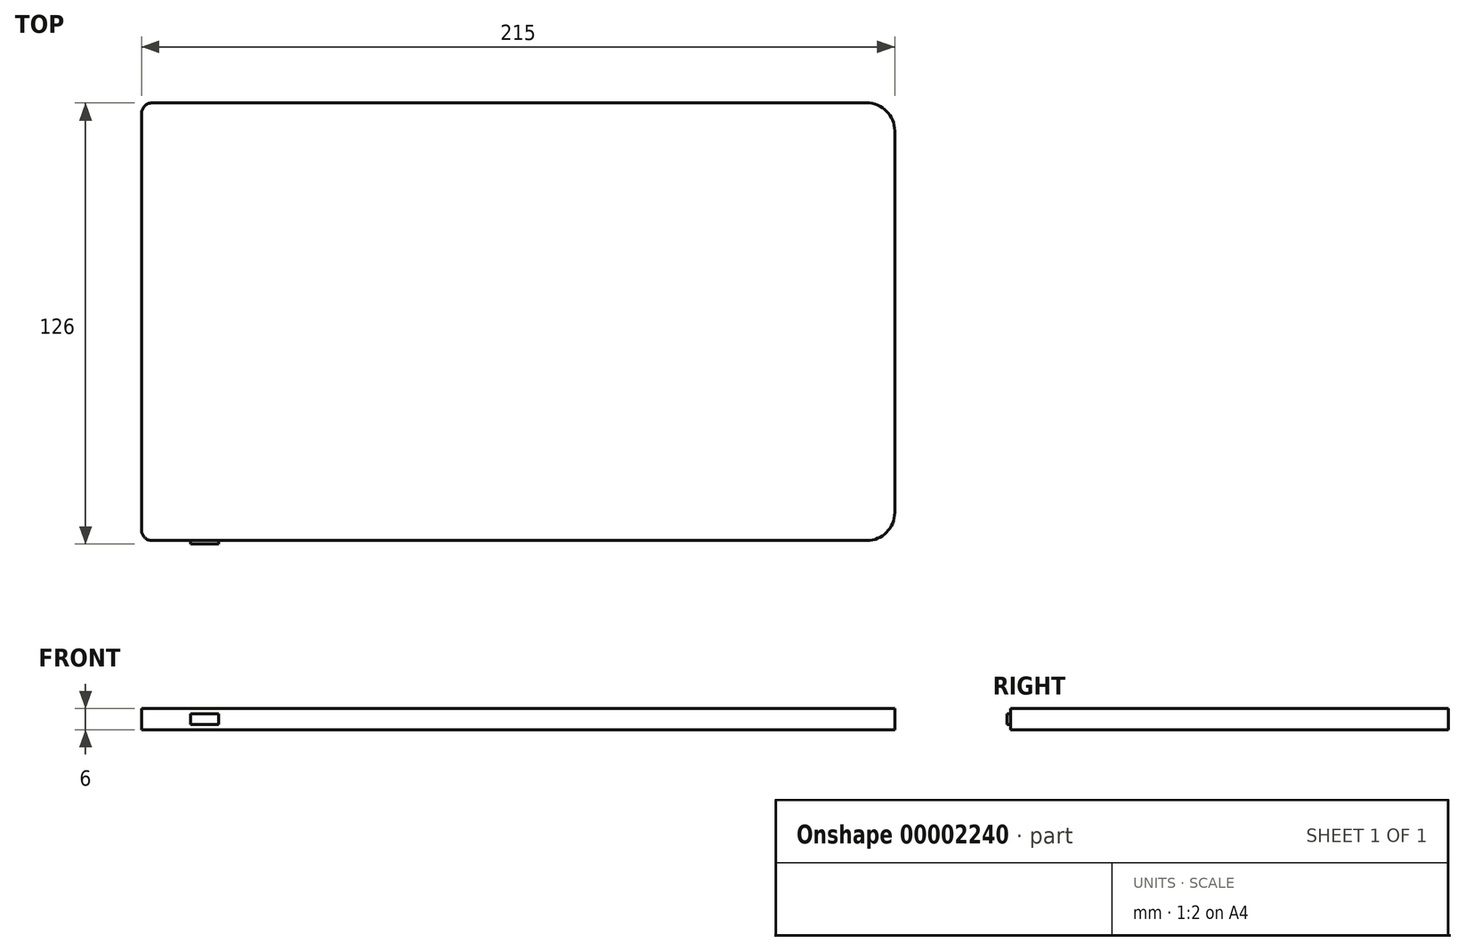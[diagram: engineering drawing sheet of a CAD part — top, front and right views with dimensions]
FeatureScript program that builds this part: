
annotation { "Feature Type Name" : "Feature", "Feature Type Description" : "" }
export const myFeature = defineFeature(function(context is Context, id is Id, definition is map)
    precondition{}
    {
        {
            var Q0;
            Q0=qCreatedBy(makeId("Top.planeOp"),FACE);
            var sketch = newSketch(context, id + "F0", { "sketchPlane" : qUnion([Q0])});
            skLineSegment(sketch, "E0.bottom", {"start": v(3, 125) * mm, "end": v(207, 125) * mm});
            skLineSegment(sketch, "E0.top", {"start": v(3, 0) * mm, "end": v(207, 0) * mm});
            skLineSegment(sketch, "E0.left", {"start": v(0, 122) * mm, "end": v(0, 3) * mm});
            skLineSegment(sketch, "E0.right", {"start": v(215, 117) * mm, "end": v(215, 8) * mm});
            skPoint(sketch, "E1.visualSharp", {"position": v(0, 125) * mm});
            skArc(sketch, "E1.filletArc", {"start": v(3, 125) * mm, "mid": v(0.88, 124.12) * mm, "end": v(0, 122) * mm});
            skPoint(sketch, "E2.visualSharp", {"position": v(0, 0) * mm});
            skArc(sketch, "E2.filletArc", {"start": v(0, 3) * mm, "mid": v(0.88, 0.88) * mm, "end": v(3, 0) * mm});
            skPoint(sketch, "E3.visualSharp", {"position": v(215, 125) * mm});
            skArc(sketch, "E3.filletArc", {"start": v(215, 117) * mm, "mid": v(212.66, 122.66) * mm, "end": v(207, 125) * mm});
            skPoint(sketch, "E4.visualSharp", {"position": v(215, 0) * mm});
            skArc(sketch, "E4.filletArc", {"start": v(207, 0) * mm, "mid": v(212.66, 2.34) * mm, "end": v(215, 8) * mm});
            skSolve(sketch);
        }
        {
            var Q0;
            Q0=makeQuery(id+"F0.imprint","IMPRINT",FACE,{"disambiguationData":[TD([[makeQuery(id+"F0.imprint","IMPRINT",EDGE,{"derivedFrom":sQuery(id+"F0.wireOp",EDGE,"E0.bottom")}),-1.0]])]});
            extrude(context, id + "F1", {"entities" : qUnion([Q0]), "depth" : 6 * mm});
        }
        {
            var Q0;
            Q0=makeQuery(id+"F1.opExtrude","SWEPT_FACE",FACE,{"disambiguationData":[OSD([sQuery(id+"F0.wireOp",EDGE,"E0.top")])]});
            var sketch = newSketch(context, id + "F2", { "sketchPlane" : qUnion([Q0])});
            skLineSegment(sketch, "E5.bottom", {"start": v(14, 4.5) * mm, "end": v(22, 4.5) * mm});
            skLineSegment(sketch, "E5.top", {"start": v(14, 1.5) * mm, "end": v(22, 1.5) * mm});
            skLineSegment(sketch, "E5.left", {"start": v(14, 4.5) * mm, "end": v(14, 1.5) * mm});
            skLineSegment(sketch, "E5.right", {"start": v(22, 4.5) * mm, "end": v(22, 1.5) * mm});
            skLineSegment(sketch, "E6", {"start": v(3, 3) * mm, "end": v(14, 3) * mm, "construction": true});
            skSolve(sketch);
        }
        {
            var Q0;
            Q0=makeQuery(id+"F2.imprint","IMPRINT",FACE,{"disambiguationData":[TD([[makeQuery(id+"F2.imprint","IMPRINT",EDGE,{"derivedFrom":sQuery(id+"F2.wireOp",EDGE,"E5.bottom")}),-1.0]])]});
            extrude(context, id + "F3", {"entities" : qUnion([Q0]), "operationType" : NewBodyOperationType.ADD, "depth" : 1 * mm});
        }
    });
